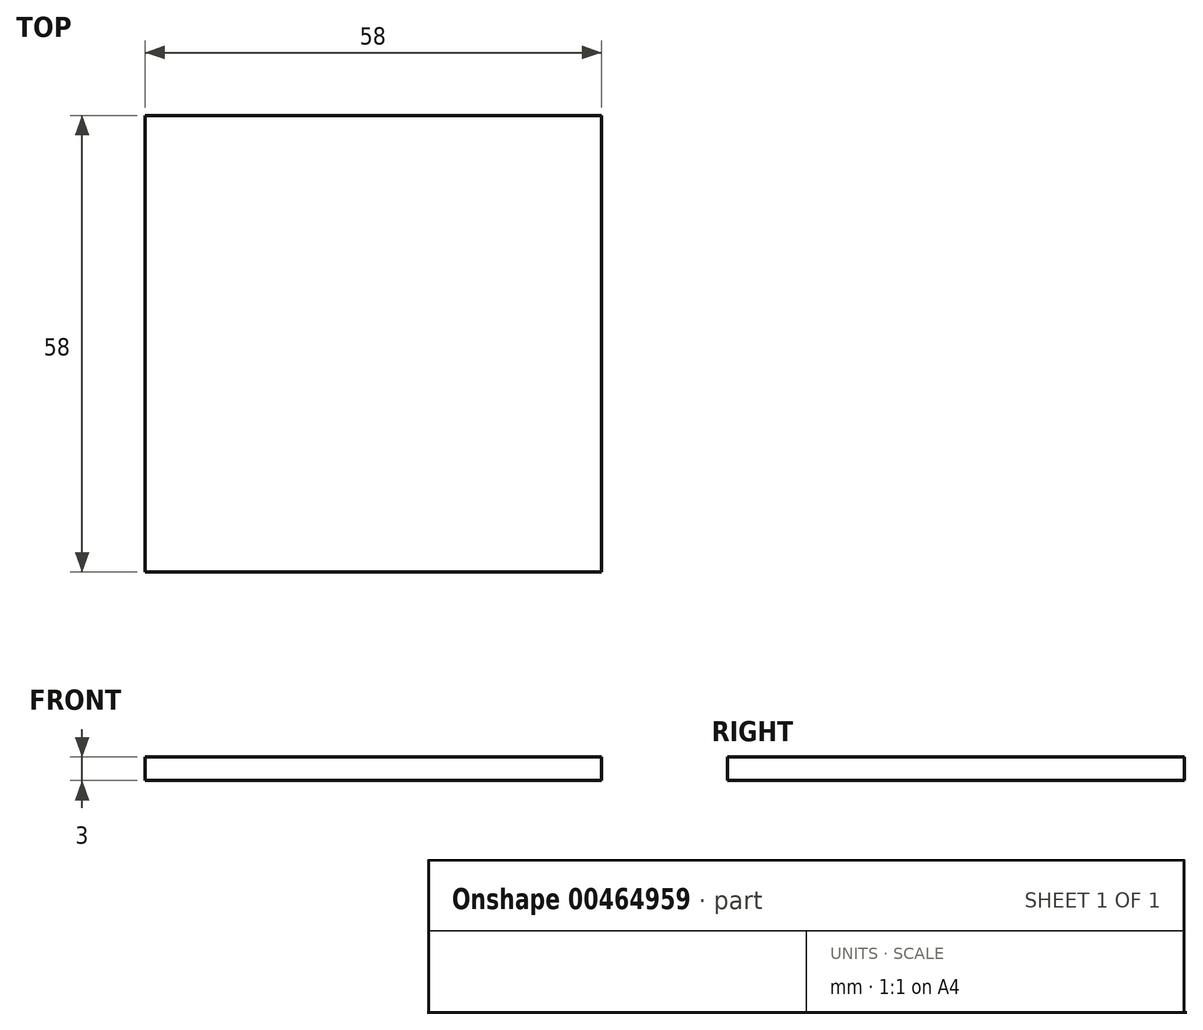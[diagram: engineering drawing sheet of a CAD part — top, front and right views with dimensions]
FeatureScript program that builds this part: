
annotation { "Feature Type Name" : "Feature", "Feature Type Description" : "" }
export const myFeature = defineFeature(function(context is Context, id is Id, definition is map)
    precondition{}
    {
        {
            var Q0;
            Q0=qCreatedBy(makeId("Top.planeOp"),FACE);
            var sketch = newSketch(context, id + "F0", { "sketchPlane" : qUnion([Q0])});
            skLineSegment(sketch, "E0.bottom", {"start": v(-29, 29) * mm, "end": v(29, 29) * mm});
            skLineSegment(sketch, "E0.top", {"start": v(-29, -29) * mm, "end": v(29, -29) * mm});
            skLineSegment(sketch, "E0.left", {"start": v(-29, 29) * mm, "end": v(-29, -29) * mm});
            skLineSegment(sketch, "E0.right", {"start": v(29, 29) * mm, "end": v(29, -29) * mm});
            skPoint(sketch, "E0.middle", {"position": v(0, 0) * mm});
            skSolve(sketch);
        }
        {
            var Q0;
            Q0=makeQuery(id+"F0.imprint","IMPRINT",FACE,{"disambiguationData":[TD([[makeQuery(id+"F0.imprint","IMPRINT",EDGE,{"derivedFrom":sQuery(id+"F0.wireOp",EDGE,"E0.bottom")}),-1.0]])]});
            extrude(context, id + "F1", {"entities" : qUnion([Q0]), "depth" : 3 * mm});
        }
    });
